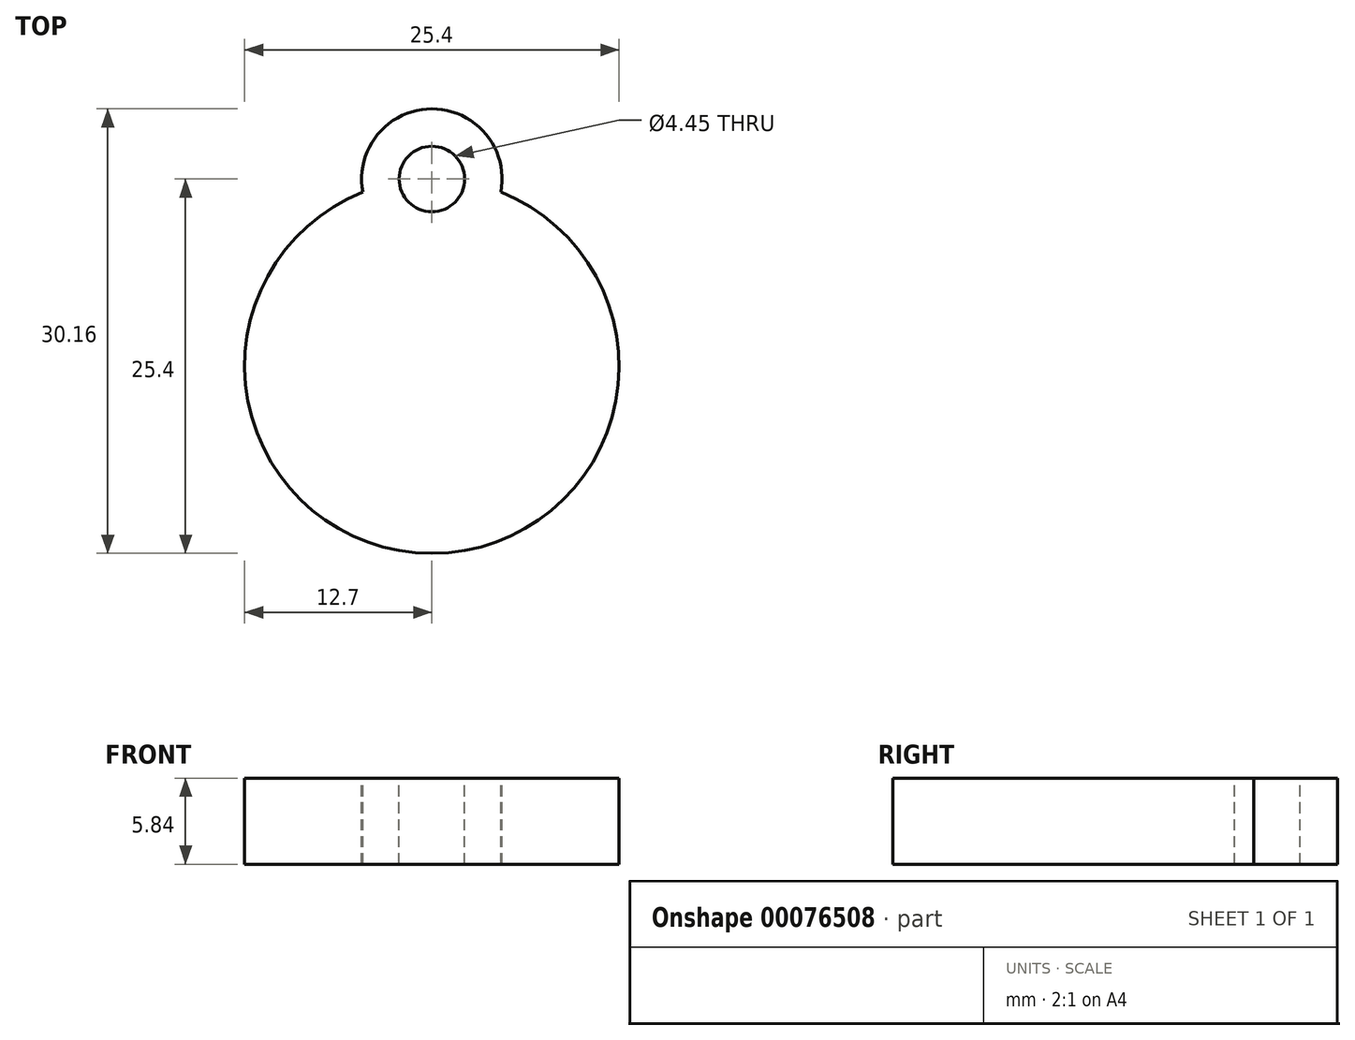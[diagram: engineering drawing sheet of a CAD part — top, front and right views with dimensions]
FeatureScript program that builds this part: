
annotation { "Feature Type Name" : "Feature", "Feature Type Description" : "" }
export const myFeature = defineFeature(function(context is Context, id is Id, definition is map)
    precondition{}
    {
        {
            var Q0;
            Q0=qCreatedBy(makeId("Top.planeOp"),FACE);
            var sketch = newSketch(context, id + "F0", { "sketchPlane" : qUnion([Q0])});
            skCircle(sketch, "E0", {"center": v(0, 0) * mm, "radius": 12.7 * mm});
            skSolve(sketch);
        }
        {
            var Q0;
            Q0=makeQuery(id+"F0.imprint","IMPRINT",FACE,{"disambiguationData":[TD([[makeQuery(id+"F0.imprint","IMPRINT",EDGE,{"derivedFrom":sQuery(id+"F0.wireOp",EDGE,"E0")}),1.0]])]});
            extrude(context, id + "F1", {"entities" : qUnion([Q0]), "depth" : 5.84 * mm});
        }
        {
            var Q0;
            Q0=makeQuery(id+"F1.opExtrude","CAP_FACE",FACE,{"disambiguationData":[OSD([sQuery(id+"F0.wireOp",EDGE,"E0")])],"isStart":false});
            var sketch = newSketch(context, id + "F2", { "sketchPlane" : qUnion([Q0])});
            skCircle(sketch, "E1", {"center": v(0, 12.7) * mm, "radius": 4.76 * mm});
            skCircle(sketch, "E2", {"center": v(0, 12.7) * mm, "radius": 2.22 * mm});
            skSolve(sketch);
        }
        {
            var Q0;
            {var subQ0=sQuery(id+"F2.wireOp",EDGE,"E1");var subQ1=makeQuery(id+"F1.opExtrude","CAP_EDGE",EDGE,{"disambiguationData":[OSD([sQuery(id+"F0.wireOp",EDGE,"E0")])],"isStart":false});var subQ2=makeQuery(id+"F2.imprint","INTERSECT",VERTEX,{"disambiguationData":[OD(0.0)],"derivedFrom":[subQ1,subQ0]});Q0=makeQuery(id+"F2.imprint","IMPRINT",FACE,{"disambiguationData":[TD([[makeQuery(id+"F2.imprint","IMPRINT",EDGE,{"disambiguationData":[TD([[subQ2,1.0]])],"derivedFrom":subQ0}),1.0]])]});}
            extrude(context, id + "F3", {"entities" : qUnion([Q0]), "operationType" : NewBodyOperationType.ADD, "oppositeDirection" : true, "depth" : 5.84 * mm});
        }
        {
            var Q0;
            {var subQ0=sQuery(id+"F2.wireOp",EDGE,"E2");var subQ1=makeQuery(id+"F1.opExtrude","CAP_EDGE",EDGE,{"disambiguationData":[OSD([sQuery(id+"F0.wireOp",EDGE,"E0")])],"isStart":false});var subQ2=makeQuery(id+"F2.imprint","INTERSECT",VERTEX,{"disambiguationData":[OD(0.0)],"derivedFrom":[subQ1,subQ0]});Q0=makeQuery(id+"F2.imprint","IMPRINT",FACE,{"disambiguationData":[TD([[makeQuery(id+"F2.imprint","IMPRINT",EDGE,{"disambiguationData":[TD([[subQ2,-1.0]])],"derivedFrom":subQ0}),1.0]])]});}
            extrude(context, id + "F4", {"entities" : qUnion([Q0]), "operationType" : NewBodyOperationType.REMOVE, "oppositeDirection" : true, "depth" : 25.4 * mm});
        }
    });
